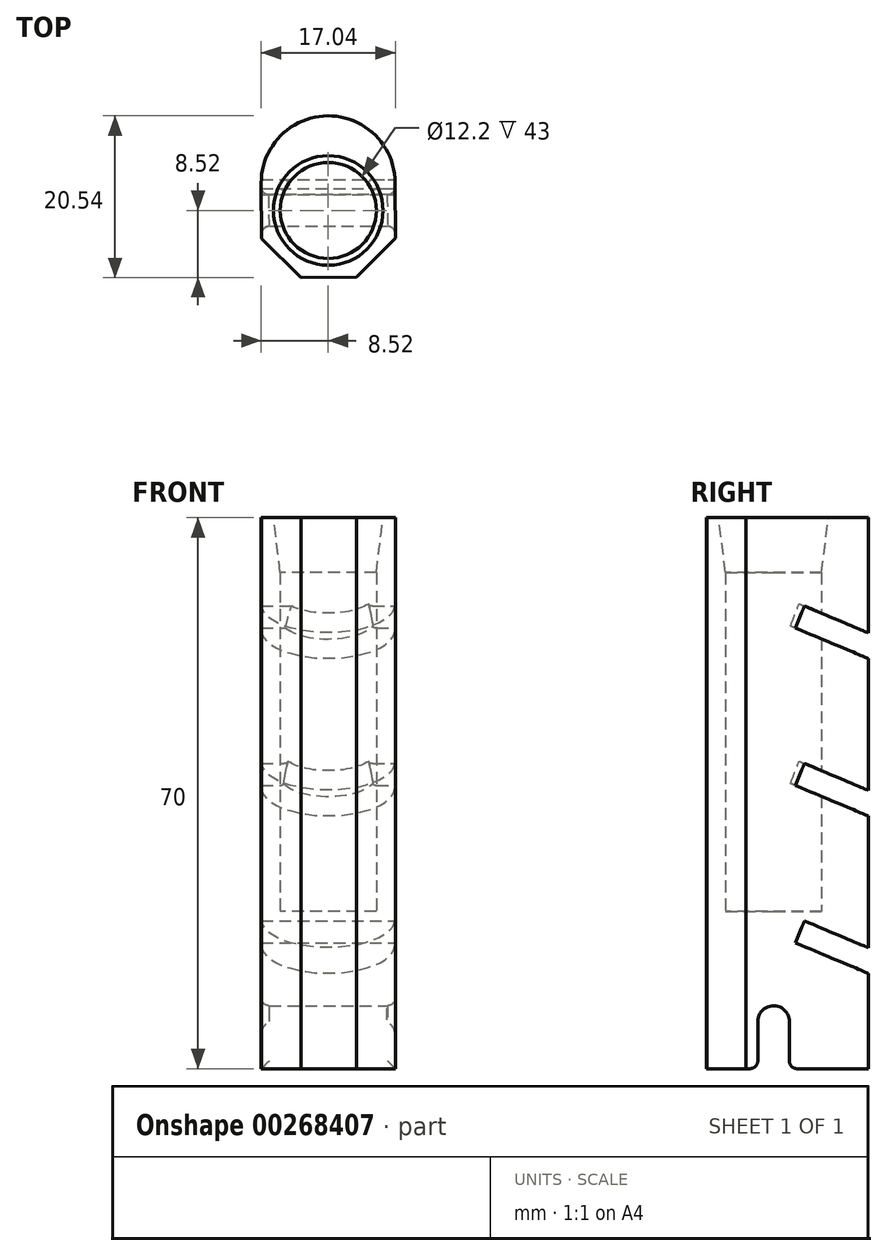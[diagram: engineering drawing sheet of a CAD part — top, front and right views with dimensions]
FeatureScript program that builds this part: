
annotation { "Feature Type Name" : "Feature", "Feature Type Description" : "" }
export const myFeature = defineFeature(function(context is Context, id is Id, definition is map)
    precondition{}
    {
        {
            var Q0;
            Q0=qCreatedBy(makeId("Top.planeOp"),FACE);
            var sketch = newSketch(context, id + "F0", { "sketchPlane" : qUnion([Q0])});
            skCircle(sketch, "E0", {"center": v(0, 0) * mm, "radius": 6.1 * mm});
            skLineSegment(sketch, "E1.2", {"start": v(8.48, 3.56) * mm, "end": v(8.52, -3.48) * mm});
            skLineSegment(sketch, "E1.3", {"start": v(8.52, -3.48) * mm, "end": v(3.56, -8.48) * mm});
            skLineSegment(sketch, "E1.4", {"start": v(3.56, -8.48) * mm, "end": v(-3.48, -8.52) * mm});
            skLineSegment(sketch, "E1.5", {"start": v(-3.48, -8.52) * mm, "end": v(-8.48, -3.56) * mm});
            skLineSegment(sketch, "E1.6", {"start": v(-8.48, -3.56) * mm, "end": v(-8.52, 3.48) * mm});
            skArc(sketch, "E2", {"start": v(8.48, 3.56) * mm, "mid": v(-0.05, 12.02) * mm, "end": v(-8.52, 3.48) * mm});
            skSolve(sketch);
        }
        {
            var Q0;
            Q0=makeQuery(id+"F0.imprint","IMPRINT",FACE,{"disambiguationData":[TD([[makeQuery(id+"F0.imprint","IMPRINT",EDGE,{"derivedFrom":sQuery(id+"F0.wireOp",EDGE,"E0")}),-1.0]])]});
            var Q1;
            Q1=makeQuery(id+"F0.imprint","IMPRINT",FACE,{"disambiguationData":[TD([[makeQuery(id+"F0.imprint","IMPRINT",EDGE,{"derivedFrom":sQuery(id+"F0.wireOp",EDGE,"E0")}),1.0]])]});
            extrude(context, id + "F1", {"entities" : qUnion([Q0, Q1]), "oppositeDirection" : true, "depth" : 20 * mm, "offsetDistance" : 25 * mm});
        }
        {
            var Q0;
            Q0=makeQuery(id+"F0.imprint","IMPRINT",FACE,{"disambiguationData":[TD([[makeQuery(id+"F0.imprint","IMPRINT",EDGE,{"derivedFrom":sQuery(id+"F0.wireOp",EDGE,"E0")}),-1.0]])]});
            extrude(context, id + "F2", {"entities" : qUnion([Q0]), "operationType" : NewBodyOperationType.ADD, "depth" : 50 * mm, "offsetDistance" : 25 * mm});
        }
        {
            var Q0;
            Q0=qCreatedBy(makeId("Right.planeOp"),FACE);
            var sketch = newSketch(context, id + "F3", { "sketchPlane" : qUnion([Q0])});
            skLineSegment(sketch, "E3", {"start": v(0, -26.52) * mm, "end": v(0, 95.47) * mm});
            skLineSegment(sketch, "E4.0", {"start": v(-12.07, -20) * mm, "end": v(9.06, -20) * mm});
            skLineSegment(sketch, "E5", {"start": v(2, -20) * mm, "end": v(-2, -20) * mm});
            skArc(sketch, "E6", {"start": v(2, -13.87) * mm, "mid": v(-0.06, -12) * mm, "end": v(-2, -14) * mm});
            skLineSegment(sketch, "E7", {"start": v(2, -20) * mm, "end": v(2, -13.87) * mm});
            skLineSegment(sketch, "E8", {"start": v(-2, -20) * mm, "end": v(-2, -14) * mm});
            skLineSegment(sketch, "E9", {"start": v(9.06, -20) * mm, "end": v(-12.07, -20) * mm});
            skSolve(sketch);
        }
        {
            var Q0;
            Q0 = qSketchRegion(id + "F3", true);
            extrude(context, id + "F4", {"entities" : qUnion([Q0]), "operationType" : NewBodyOperationType.REMOVE, "oppositeDirection" : true, "depth" : 25 * mm, "offsetDistance" : 25 * mm, "symmetric" : true});
        }
        {
            var Q0;
            Q0=makeQuery(id+"F4.boolean.opBoolean","COPY",EDGE,{"derivedFrom":makeQuery(id+"F4.opExtrude","CAP_EDGE",EDGE,{"disambiguationData":[OSD([sQuery(id+"F3.wireOp",EDGE,"E8")]),topologyDisambiguationEdgeConnected([makeQuery(id+"F1.opExtrude","CAP_FACE",FACE,{"disambiguationData":[OSD([sQuery(id+"F0.wireOp",EDGE,"1uds2ZHc-WtPi-VxFk-JlT4-WQfVxmiHtsB6")])],"isStart":false})])],"isStart":false})});
            var Q1;
            Q1=makeQuery(id+"F4.boolean.opBoolean","COPY",EDGE,{"derivedFrom":makeQuery(id+"F4.opExtrude","CAP_EDGE",EDGE,{"disambiguationData":[OSD([sQuery(id+"F3.wireOp",EDGE,"E7")]),topologyDisambiguationEdgeConnected([makeQuery(id+"F1.opExtrude","CAP_FACE",FACE,{"disambiguationData":[OSD([sQuery(id+"F0.wireOp",EDGE,"1uds2ZHc-WtPi-VxFk-JlT4-WQfVxmiHtsB6")])],"isStart":false})])],"isStart":false})});
            var Q2;
            Q2=makeQuery(id+"F4.boolean.opBoolean","COPY",EDGE,{"derivedFrom":makeQuery(id+"F4.opExtrude","CAP_EDGE",EDGE,{"disambiguationData":[OSD([sQuery(id+"F3.wireOp",EDGE,"E6")]),OD(1.0)],"isStart":false})});
            var Q3;
            Q3=makeQuery(id+"F4.boolean.opBoolean","COPY",EDGE,{"derivedFrom":makeQuery(id+"F4.opExtrude","CAP_EDGE",EDGE,{"disambiguationData":[OSD([sQuery(id+"F3.wireOp",EDGE,"E6")]),OD(0.0)],"isStart":false})});
            var Q4;
            Q4=makeQuery(id+"F2.opExtrude","CAP_EDGE",EDGE,{"disambiguationData":[OSD([sQuery(id+"F0.wireOp",EDGE,"1uds2ZHc-WtPi-VxFk-JlT4-WQfVxmiHtsB6")])],"isStart":false});
            var Q5;
            {var subQ0=sQuery(id+"F0.wireOp",EDGE,"1uds2ZHc-WtPi-VxFk-JlT4-WQfVxmiHtsB6");Q5=makeQuery(id+"F4.boolean.opBoolean","SPLIT",EDGE,{"disambiguationData":[TD([makeQuery(id+"F4.opExtrude","SWEPT_FACE",FACE,{"disambiguationData":[OSD([sQuery(id+"F3.wireOp",EDGE,"E8")])]})])],"derivedFrom":makeQuery(id+"F1.opExtrude","CAP_EDGE",EDGE,{"disambiguationData":[OSD([subQ0])],"isStart":false})});}
            var Q6;
            {var subQ0=sQuery(id+"F0.wireOp",EDGE,"1uds2ZHc-WtPi-VxFk-JlT4-WQfVxmiHtsB6");Q6=makeQuery(id+"F4.boolean.opBoolean","SPLIT",EDGE,{"disambiguationData":[TD([makeQuery(id+"F4.opExtrude","SWEPT_FACE",FACE,{"disambiguationData":[OSD([sQuery(id+"F3.wireOp",EDGE,"E7")])]})])],"derivedFrom":makeQuery(id+"F1.opExtrude","CAP_EDGE",EDGE,{"disambiguationData":[OSD([subQ0])],"isStart":false})});}
            var Q7;
            {var subQ0=sQuery(id+"F0.wireOp",EDGE,"E1.5");Q7=makeQuery(id+"F4.boolean.opBoolean","INTERSECT",EDGE,{"derivedFrom":[makeQuery(id+"F2.boolean.opBoolean","MERGE",FACE,{"derivedFrom":[makeQuery(id+"F1.opExtrude","SWEPT_FACE",FACE,{"disambiguationData":[OSD([subQ0])]}),makeQuery(id+"F2.opExtrude","SWEPT_FACE",FACE,{"disambiguationData":[OSD([subQ0])]})]}),makeQuery(id+"F4.opExtrude","SWEPT_FACE",FACE,{"disambiguationData":[OSD([sQuery(id+"F3.wireOp",EDGE,"E6")])]})]});}
            var Q8;
            Q8=makeQuery(id+"F4.boolean.opBoolean","COPY",FACE,{"derivedFrom":makeQuery(id+"F4.opExtrude","SWEPT_FACE",FACE,{"disambiguationData":[OSD([sQuery(id+"F3.wireOp",EDGE,"E6")])]})});
            var Q9;
            Q9=makeQuery(id+"F4.boolean.opBoolean","INTERSECT",EDGE,{"derivedFrom":[makeQuery(id+"F1.opExtrude","CAP_FACE",FACE,{"disambiguationData":[OSD([sQuery(id+"F0.wireOp",EDGE,"E1.0"),sQuery(id+"F0.wireOp",EDGE,"E1.1"),sQuery(id+"F0.wireOp",EDGE,"E1.2"),sQuery(id+"F0.wireOp",EDGE,"E1.3"),sQuery(id+"F0.wireOp",EDGE,"E1.4"),sQuery(id+"F0.wireOp",EDGE,"E1.5"),sQuery(id+"F0.wireOp",EDGE,"E1.6"),sQuery(id+"F0.wireOp",EDGE,"E1.7")])],"isStart":false}),makeQuery(id+"F4.opExtrude","SWEPT_FACE",FACE,{"disambiguationData":[OSD([sQuery(id+"F3.wireOp",EDGE,"E8")])]})]});
            var Q10;
            Q10=makeQuery(id+"F4.boolean.opBoolean","INTERSECT",EDGE,{"derivedFrom":[makeQuery(id+"F1.opExtrude","CAP_FACE",FACE,{"disambiguationData":[OSD([sQuery(id+"F0.wireOp",EDGE,"E1.0"),sQuery(id+"F0.wireOp",EDGE,"E1.1"),sQuery(id+"F0.wireOp",EDGE,"E1.2"),sQuery(id+"F0.wireOp",EDGE,"E1.3"),sQuery(id+"F0.wireOp",EDGE,"E1.4"),sQuery(id+"F0.wireOp",EDGE,"E1.5"),sQuery(id+"F0.wireOp",EDGE,"E1.6"),sQuery(id+"F0.wireOp",EDGE,"E1.7")])],"isStart":false}),makeQuery(id+"F4.opExtrude","SWEPT_FACE",FACE,{"disambiguationData":[OSD([sQuery(id+"F3.wireOp",EDGE,"E7")])]})]});
            fillet(context, id + "F5", {"entities" : qUnion([Q0, Q1, Q2, Q3, Q4, Q5, Q6, Q7, Q8, Q9, Q10]), "radius" : 1 * mm, "tangentPropagation" : true, "allowEdgeOverflow" : false});
        }
        {
            var Q0;
            Q0=qCreatedBy(makeId("Right.planeOp"),FACE);
            var sketch = newSketch(context, id + "F6", { "sketchPlane" : qUnion([Q0])});
            skLineSegment(sketch, "E10", {"start": v(12.9, -8.26) * mm, "end": v(14.07, -5.49) * mm});
            skLineSegment(sketch, "E11", {"start": v(14.07, -5.49) * mm, "end": v(3.93, -1.23) * mm});
            skLineSegment(sketch, "E12", {"start": v(2.77, -4) * mm, "end": v(3.93, -1.23) * mm});
            skLineSegment(sketch, "E13", {"start": v(2.77, -4) * mm, "end": v(12.9, -8.26) * mm});
            skLineSegment(sketch, "E14.0.1.0", {"start": v(14.07, 14.51) * mm, "end": v(3.93, 18.77) * mm});
            skLineSegment(sketch, "E14.0.1.1", {"start": v(12.9, 11.74) * mm, "end": v(14.07, 14.51) * mm});
            skLineSegment(sketch, "E14.0.1.2", {"start": v(2.77, 16) * mm, "end": v(12.9, 11.74) * mm});
            skLineSegment(sketch, "E14.0.1.3", {"start": v(2.77, 16) * mm, "end": v(3.93, 18.77) * mm});
            skLineSegment(sketch, "E14.0.2.0", {"start": v(14.07, 34.51) * mm, "end": v(3.93, 38.77) * mm});
            skLineSegment(sketch, "E14.0.2.1", {"start": v(12.9, 31.74) * mm, "end": v(14.07, 34.51) * mm});
            skLineSegment(sketch, "E14.0.2.2", {"start": v(2.77, 36) * mm, "end": v(12.9, 31.74) * mm});
            skLineSegment(sketch, "E14.0.2.3", {"start": v(2.77, 36) * mm, "end": v(3.93, 38.77) * mm});
            skLineSegment(sketch, "E14.direction2", {"start": v(3.93, -1.23) * mm, "end": v(3.93, 18.77) * mm, "construction": true});
            skSolve(sketch);
        }
        {
            var Q0;
            Q0=makeQuery(id+"F6.imprint","IMPRINT",FACE,{"disambiguationData":[TD([[makeQuery(id+"F6.imprint","IMPRINT",EDGE,{"derivedFrom":sQuery(id+"F6.wireOp",EDGE,"E14.0.2.0")}),1.0]])]});
            var Q1;
            Q1=makeQuery(id+"F6.imprint","IMPRINT",FACE,{"disambiguationData":[TD([[makeQuery(id+"F6.imprint","IMPRINT",EDGE,{"derivedFrom":sQuery(id+"F6.wireOp",EDGE,"E14.0.1.0")}),1.0]])]});
            var Q2;
            Q2=makeQuery(id+"F6.imprint","IMPRINT",FACE,{"disambiguationData":[TD([[makeQuery(id+"F6.imprint","IMPRINT",EDGE,{"derivedFrom":sQuery(id+"F6.wireOp",EDGE,"E10")}),1.0]])]});
            extrude(context, id + "F7", {"entities" : qUnion([Q0, Q1, Q2]), "operationType" : NewBodyOperationType.REMOVE, "oppositeDirection" : true, "depth" : 25 * mm, "offsetDistance" : 25 * mm, "hasSecondDirection" : true, "secondDirectionOppositeDirection" : false, "secondDirectionDepth" : 25 * mm});
        }
        {
            var Q0;
            {var subQ0=sQuery(id+"F0.wireOp",EDGE,"1uds2ZHc-WtPi-VxFk-JlT4-WQfVxmiHtsB6");Q0=makeQuery(id+"F7.boolean.opBoolean","INTERSECT",EDGE,{"derivedFrom":[makeQuery(id+"F2.boolean.opBoolean","MERGE",FACE,{"derivedFrom":[makeQuery(id+"F1.opExtrude","SWEPT_FACE",FACE,{"disambiguationData":[OSD([subQ0])]}),makeQuery(id+"F2.opExtrude","SWEPT_FACE",FACE,{"disambiguationData":[OSD([subQ0])]})]}),makeQuery(id+"F7.opExtrude","SWEPT_FACE",FACE,{"disambiguationData":[OSD([sQuery(id+"F6.wireOp",EDGE,"E14.0.2.0")])]})]});}
            var Q1;
            {var subQ0=sQuery(id+"F0.wireOp",EDGE,"1uds2ZHc-WtPi-VxFk-JlT4-WQfVxmiHtsB6");Q1=makeQuery(id+"F7.boolean.opBoolean","INTERSECT",EDGE,{"derivedFrom":[makeQuery(id+"F2.boolean.opBoolean","MERGE",FACE,{"derivedFrom":[makeQuery(id+"F1.opExtrude","SWEPT_FACE",FACE,{"disambiguationData":[OSD([subQ0])]}),makeQuery(id+"F2.opExtrude","SWEPT_FACE",FACE,{"disambiguationData":[OSD([subQ0])]})]}),makeQuery(id+"F7.opExtrude","SWEPT_FACE",FACE,{"disambiguationData":[OSD([sQuery(id+"F6.wireOp",EDGE,"E14.0.2.2")])]})]});}
            var Q2;
            {var subQ0=sQuery(id+"F0.wireOp",EDGE,"1uds2ZHc-WtPi-VxFk-JlT4-WQfVxmiHtsB6");Q2=makeQuery(id+"F7.boolean.opBoolean","INTERSECT",EDGE,{"derivedFrom":[makeQuery(id+"F2.boolean.opBoolean","MERGE",FACE,{"derivedFrom":[makeQuery(id+"F1.opExtrude","SWEPT_FACE",FACE,{"disambiguationData":[OSD([subQ0])]}),makeQuery(id+"F2.opExtrude","SWEPT_FACE",FACE,{"disambiguationData":[OSD([subQ0])]})]}),makeQuery(id+"F7.opExtrude","SWEPT_FACE",FACE,{"disambiguationData":[OSD([sQuery(id+"F6.wireOp",EDGE,"E14.0.1.0")])]})]});}
            var Q3;
            {var subQ0=sQuery(id+"F0.wireOp",EDGE,"1uds2ZHc-WtPi-VxFk-JlT4-WQfVxmiHtsB6");Q3=makeQuery(id+"F7.boolean.opBoolean","INTERSECT",EDGE,{"derivedFrom":[makeQuery(id+"F2.boolean.opBoolean","MERGE",FACE,{"derivedFrom":[makeQuery(id+"F1.opExtrude","SWEPT_FACE",FACE,{"disambiguationData":[OSD([subQ0])]}),makeQuery(id+"F2.opExtrude","SWEPT_FACE",FACE,{"disambiguationData":[OSD([subQ0])]})]}),makeQuery(id+"F7.opExtrude","SWEPT_FACE",FACE,{"disambiguationData":[OSD([sQuery(id+"F6.wireOp",EDGE,"E14.0.1.2")])]})]});}
            var Q4;
            {var subQ0=sQuery(id+"F0.wireOp",EDGE,"1uds2ZHc-WtPi-VxFk-JlT4-WQfVxmiHtsB6");Q4=makeQuery(id+"F7.boolean.opBoolean","INTERSECT",EDGE,{"derivedFrom":[makeQuery(id+"F2.boolean.opBoolean","MERGE",FACE,{"derivedFrom":[makeQuery(id+"F1.opExtrude","SWEPT_FACE",FACE,{"disambiguationData":[OSD([subQ0])]}),makeQuery(id+"F2.opExtrude","SWEPT_FACE",FACE,{"disambiguationData":[OSD([subQ0])]})]}),makeQuery(id+"F7.opExtrude","SWEPT_FACE",FACE,{"disambiguationData":[OSD([sQuery(id+"F6.wireOp",EDGE,"E11")])]})]});}
            var Q5;
            {var subQ0=sQuery(id+"F0.wireOp",EDGE,"1uds2ZHc-WtPi-VxFk-JlT4-WQfVxmiHtsB6");Q5=makeQuery(id+"F7.boolean.opBoolean","INTERSECT",EDGE,{"derivedFrom":[makeQuery(id+"F2.boolean.opBoolean","MERGE",FACE,{"derivedFrom":[makeQuery(id+"F1.opExtrude","SWEPT_FACE",FACE,{"disambiguationData":[OSD([subQ0])]}),makeQuery(id+"F2.opExtrude","SWEPT_FACE",FACE,{"disambiguationData":[OSD([subQ0])]})]}),makeQuery(id+"F7.opExtrude","SWEPT_FACE",FACE,{"disambiguationData":[OSD([sQuery(id+"F6.wireOp",EDGE,"E13")])]})]});}
            var Q6;
            {var subQ0=sQuery(id+"F0.wireOp",EDGE,"1uds2ZHc-WtPi-VxFk-JlT4-WQfVxmiHtsB6");Q6=makeQuery(id+"F7.boolean.opBoolean","INTERSECT",EDGE,{"disambiguationData":[OD(0.0)],"derivedFrom":[makeQuery(id+"F2.boolean.opBoolean","MERGE",FACE,{"derivedFrom":[makeQuery(id+"F1.opExtrude","SWEPT_FACE",FACE,{"disambiguationData":[OSD([subQ0])]}),makeQuery(id+"F2.opExtrude","SWEPT_FACE",FACE,{"disambiguationData":[OSD([subQ0])]})]}),makeQuery(id+"F7.opExtrude","SWEPT_FACE",FACE,{"disambiguationData":[OSD([sQuery(id+"F6.wireOp",EDGE,"E14.0.1.3")])]})]});}
            var Q7;
            {var subQ0=sQuery(id+"F0.wireOp",EDGE,"1uds2ZHc-WtPi-VxFk-JlT4-WQfVxmiHtsB6");Q7=makeQuery(id+"F7.boolean.opBoolean","INTERSECT",EDGE,{"disambiguationData":[OD(0.0)],"derivedFrom":[makeQuery(id+"F2.boolean.opBoolean","MERGE",FACE,{"derivedFrom":[makeQuery(id+"F1.opExtrude","SWEPT_FACE",FACE,{"disambiguationData":[OSD([subQ0])]}),makeQuery(id+"F2.opExtrude","SWEPT_FACE",FACE,{"disambiguationData":[OSD([subQ0])]})]}),makeQuery(id+"F7.opExtrude","SWEPT_FACE",FACE,{"disambiguationData":[OSD([sQuery(id+"F6.wireOp",EDGE,"E14.0.2.3")])]})]});}
            var Q8;
            {var subQ0=sQuery(id+"F0.wireOp",EDGE,"1uds2ZHc-WtPi-VxFk-JlT4-WQfVxmiHtsB6");Q8=makeQuery(id+"F7.boolean.opBoolean","INTERSECT",EDGE,{"disambiguationData":[OD(1.0)],"derivedFrom":[makeQuery(id+"F2.boolean.opBoolean","MERGE",FACE,{"derivedFrom":[makeQuery(id+"F1.opExtrude","SWEPT_FACE",FACE,{"disambiguationData":[OSD([subQ0])]}),makeQuery(id+"F2.opExtrude","SWEPT_FACE",FACE,{"disambiguationData":[OSD([subQ0])]})]}),makeQuery(id+"F7.opExtrude","SWEPT_FACE",FACE,{"disambiguationData":[OSD([sQuery(id+"F6.wireOp",EDGE,"E14.0.2.3")])]})]});}
            var Q9;
            Q9=makeQuery(id+"F7.boolean.opBoolean","INTERSECT",EDGE,{"disambiguationData":[OD(0.0)],"derivedFrom":[makeQuery(id+"F2.opExtrude","SWEPT_FACE",FACE,{"disambiguationData":[OSD([sQuery(id+"F0.wireOp",EDGE,"E0")])]}),makeQuery(id+"F7.opExtrude","SWEPT_FACE",FACE,{"disambiguationData":[OSD([sQuery(id+"F6.wireOp",EDGE,"E14.0.2.3")])]})]});
            var Q10;
            Q10=makeQuery(id+"F7.boolean.opBoolean","INTERSECT",EDGE,{"disambiguationData":[OD(0.0)],"derivedFrom":[makeQuery(id+"F2.opExtrude","SWEPT_FACE",FACE,{"disambiguationData":[OSD([sQuery(id+"F0.wireOp",EDGE,"E0")])]}),makeQuery(id+"F7.opExtrude","SWEPT_FACE",FACE,{"disambiguationData":[OSD([sQuery(id+"F6.wireOp",EDGE,"E14.0.1.3")])]})]});
            var Q11;
            Q11=makeQuery(id+"F7.boolean.opBoolean","INTERSECT",EDGE,{"disambiguationData":[OD(1.0)],"derivedFrom":[makeQuery(id+"F2.opExtrude","SWEPT_FACE",FACE,{"disambiguationData":[OSD([sQuery(id+"F0.wireOp",EDGE,"E0")])]}),makeQuery(id+"F7.opExtrude","SWEPT_FACE",FACE,{"disambiguationData":[OSD([sQuery(id+"F6.wireOp",EDGE,"E14.0.1.3")])]})]});
            var Q12;
            {var subQ0=sQuery(id+"F0.wireOp",EDGE,"1uds2ZHc-WtPi-VxFk-JlT4-WQfVxmiHtsB6");Q12=makeQuery(id+"F7.boolean.opBoolean","INTERSECT",EDGE,{"disambiguationData":[OD(1.0)],"derivedFrom":[makeQuery(id+"F2.boolean.opBoolean","MERGE",FACE,{"derivedFrom":[makeQuery(id+"F1.opExtrude","SWEPT_FACE",FACE,{"disambiguationData":[OSD([subQ0])]}),makeQuery(id+"F2.opExtrude","SWEPT_FACE",FACE,{"disambiguationData":[OSD([subQ0])]})]}),makeQuery(id+"F7.opExtrude","SWEPT_FACE",FACE,{"disambiguationData":[OSD([sQuery(id+"F6.wireOp",EDGE,"E12")])]})]});}
            var Q13;
            {var subQ0=sQuery(id+"F0.wireOp",EDGE,"1uds2ZHc-WtPi-VxFk-JlT4-WQfVxmiHtsB6");Q13=makeQuery(id+"F7.boolean.opBoolean","INTERSECT",EDGE,{"disambiguationData":[OD(0.0)],"derivedFrom":[makeQuery(id+"F2.boolean.opBoolean","MERGE",FACE,{"derivedFrom":[makeQuery(id+"F1.opExtrude","SWEPT_FACE",FACE,{"disambiguationData":[OSD([subQ0])]}),makeQuery(id+"F2.opExtrude","SWEPT_FACE",FACE,{"disambiguationData":[OSD([subQ0])]})]}),makeQuery(id+"F7.opExtrude","SWEPT_FACE",FACE,{"disambiguationData":[OSD([sQuery(id+"F6.wireOp",EDGE,"E12")])]})]});}
            fillet(context, id + "F8", {"entities" : qUnion([Q0, Q1, Q2, Q3, Q4, Q5, Q6, Q7, Q8, Q9, Q10, Q11, Q12, Q13]), "radius" : 0.5 * mm, "tangentPropagation" : true, "allowEdgeOverflow" : false});
        }
        {
            var Q0;
            Q0=makeQuery(id+"F2.opExtrude","CAP_EDGE",EDGE,{"disambiguationData":[OSD([sQuery(id+"F0.wireOp",EDGE,"E0")])],"isStart":false});
            chamfer(context, id + "F9", {"entities" : qUnion([Q0]), "chamferType" : ChamferType.OFFSET_ANGLE, "width" : 7 * mm, "oppositeDirection" : false, "angle" : 7 * degree, "tangentPropagation" : true});
        }
    });
